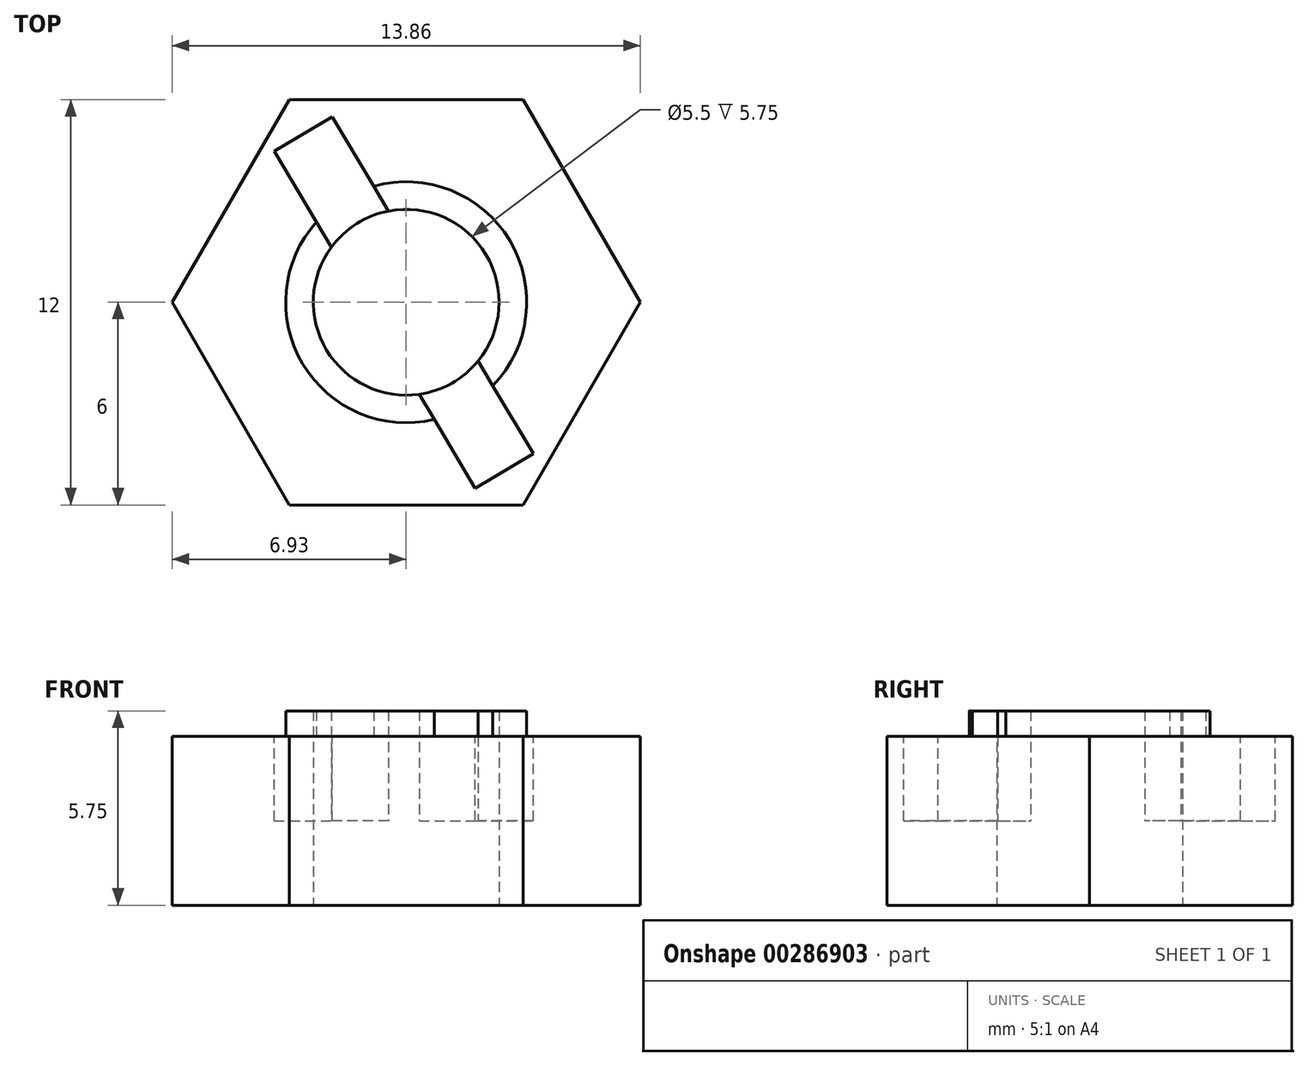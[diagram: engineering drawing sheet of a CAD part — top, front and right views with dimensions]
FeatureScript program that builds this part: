
annotation { "Feature Type Name" : "Feature", "Feature Type Description" : "" }
export const myFeature = defineFeature(function(context is Context, id is Id, definition is map)
    precondition{}
    {
        {
            var Q0;
            Q0=qCreatedBy(makeId("Top.planeOp"),FACE);
            var sketch = newSketch(context, id + "F0", { "sketchPlane" : qUnion([Q0])});
            skCircle(sketch, "E0.cCircle", {"center": v(0, 0) * mm, "radius": 6 * mm, "construction": true});
            skLineSegment(sketch, "E0.0", {"start": v(-3.46, 6) * mm, "end": v(3.46, 6) * mm});
            skLineSegment(sketch, "E0.1", {"start": v(3.46, 6) * mm, "end": v(6.93, 0) * mm});
            skLineSegment(sketch, "E0.2", {"start": v(6.93, 0) * mm, "end": v(3.46, -6) * mm});
            skLineSegment(sketch, "E0.3", {"start": v(3.46, -6) * mm, "end": v(-3.46, -6) * mm});
            skLineSegment(sketch, "E0.4", {"start": v(-3.46, -6) * mm, "end": v(-6.93, 0) * mm});
            skLineSegment(sketch, "E0.5", {"start": v(-6.93, 0) * mm, "end": v(-3.46, 6) * mm});
            skPoint(sketch, "E0.0.midPoint", {"position": v(0, 6) * mm});
            skCircle(sketch, "E1", {"center": v(0, 0) * mm, "radius": 2.75 * mm});
            skSolve(sketch);
        }
        {
            var Q0;
            Q0 = qSketchRegion(id + "F0", true);
            extrude(context, id + "F1", {"entities" : qUnion([Q0]), "depth" : 5 * mm});
        }
        {
            var Q0;
            Q0=makeQuery(id+"F1.opExtrude","CAP_FACE",FACE,{"disambiguationData":[OSD([sQuery(id+"F0.wireOp",EDGE,"E0.0"),sQuery(id+"F0.wireOp",EDGE,"E0.1"),sQuery(id+"F0.wireOp",EDGE,"E0.2"),sQuery(id+"F0.wireOp",EDGE,"E0.3"),sQuery(id+"F0.wireOp",EDGE,"E0.4"),sQuery(id+"F0.wireOp",EDGE,"E0.5"),sQuery(id+"F0.wireOp",EDGE,"E1")])],"isStart":false});
            var sketch = newSketch(context, id + "F2", { "sketchPlane" : qUnion([Q0])});
            skCircle(sketch, "E2", {"center": v(0, 0) * mm, "radius": 3.57 * mm});
            skSolve(sketch);
        }
        {
            var Q0;
            Q0=makeQuery(id+"F2.imprint","IMPRINT",FACE,{"disambiguationData":[TD([[makeQuery(id+"F2.imprint","IMPRINT",EDGE,{"derivedFrom":sQuery(id+"F2.wireOp",EDGE,"E2")}),1.0]])]});
            extrude(context, id + "F3", {"entities" : qUnion([Q0]), "operationType" : NewBodyOperationType.ADD, "depth" : .75 * mm});
        }
        {
            var Q0;
            Q0=makeQuery(id+"F1.opExtrude","CAP_FACE",FACE,{"disambiguationData":[OSD([sQuery(id+"F0.wireOp",EDGE,"E0.0"),sQuery(id+"F0.wireOp",EDGE,"E0.1"),sQuery(id+"F0.wireOp",EDGE,"E0.2"),sQuery(id+"F0.wireOp",EDGE,"E0.3"),sQuery(id+"F0.wireOp",EDGE,"E0.4"),sQuery(id+"F0.wireOp",EDGE,"E0.5"),sQuery(id+"F0.wireOp",EDGE,"E1")])],"isStart":false});
            var sketch = newSketch(context, id + "F4", { "sketchPlane" : qUnion([Q0])});
            skLineSegment(sketch, "E3", {"start": v(-3.9, 4.47) * mm, "end": v(2.04, -5.5) * mm});
            skLineSegment(sketch, "E4", {"start": v(3.76, -4.48) * mm, "end": v(-2.19, 5.5) * mm});
            skLineSegment(sketch, "E5", {"start": v(-3.9, 4.47) * mm, "end": v(-2.19, 5.5) * mm});
            skLineSegment(sketch, "E6", {"start": v(2.04, -5.5) * mm, "end": v(3.76, -4.48) * mm});
            skSolve(sketch);
        }
        {
            var Q0;
            Q0 = qSketchRegion(id + "F4", true);
            extrude(context, id + "F5", {"entities" : qUnion([Q0]), "operationType" : NewBodyOperationType.REMOVE, "oppositeDirection" : true, "depth" : 2.5 * mm});
        }
        {
            var Q0;
            Q0=makeQuery(id+"F5.boolean.opBoolean","COPY",FACE,{"disambiguationData":[OD(0.0)],"derivedFrom":makeQuery(id+"F5.opExtrude","CAP_FACE",FACE,{"disambiguationData":[OSD([sQuery(id+"F4.wireOp",EDGE,"E3"),sQuery(id+"F4.wireOp",EDGE,"E4"),sQuery(id+"F4.wireOp",EDGE,"E5"),sQuery(id+"F4.wireOp",EDGE,"E6")])],"isStart":true})});
            var Q1;
            Q1=makeQuery(id+"F5.boolean.opBoolean","COPY",FACE,{"disambiguationData":[OD(1.0)],"derivedFrom":makeQuery(id+"F5.opExtrude","CAP_FACE",FACE,{"disambiguationData":[OSD([sQuery(id+"F4.wireOp",EDGE,"E3"),sQuery(id+"F4.wireOp",EDGE,"E4"),sQuery(id+"F4.wireOp",EDGE,"E5"),sQuery(id+"F4.wireOp",EDGE,"E6")])],"isStart":true})});
            extrude(context, id + "F6", {"entities" : qUnion([Q0, Q1]), "operationType" : NewBodyOperationType.REMOVE, "oppositeDirection" : true, "depth" : 25 * mm});
        }
    });
